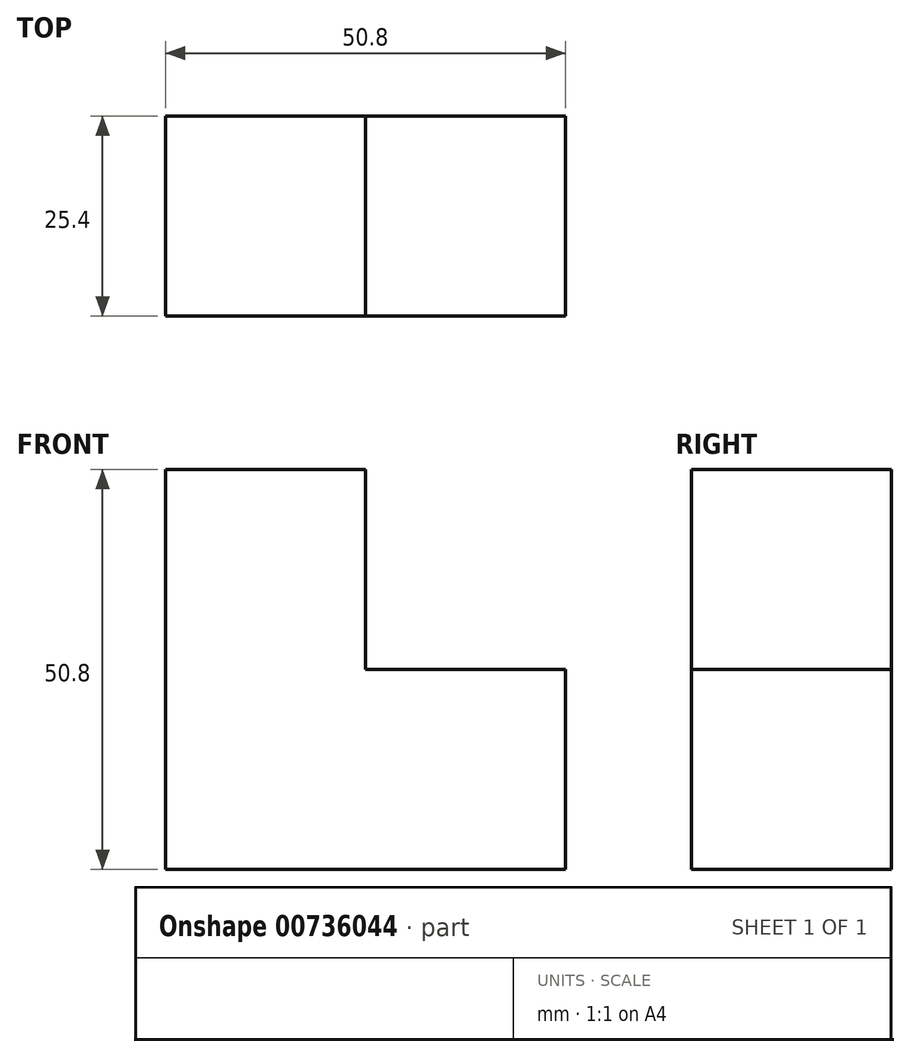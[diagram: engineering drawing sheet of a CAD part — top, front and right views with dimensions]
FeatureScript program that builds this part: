
annotation { "Feature Type Name" : "Feature", "Feature Type Description" : "" }
export const myFeature = defineFeature(function(context is Context, id is Id, definition is map)
    precondition{}
    {
        {
            var Q0;
            Q0=qCreatedBy(makeId("Front.planeOp"),FACE);
            var sketch = newSketch(context, id + "F0", { "sketchPlane" : qUnion([Q0])});
            skLineSegment(sketch, "E0", {"start": v(-41.15, 50.8) * mm, "end": v(-41.15, 0) * mm});
            skLineSegment(sketch, "E1", {"start": v(-41.15, 0) * mm, "end": v(9.65, 0) * mm});
            skLineSegment(sketch, "E2", {"start": v(-41.15, 50.8) * mm, "end": v(-15.75, 50.8) * mm});
            skLineSegment(sketch, "E3", {"start": v(-15.75, 50.8) * mm, "end": v(-15.75, 25.4) * mm});
            skLineSegment(sketch, "E4", {"start": v(-15.75, 25.4) * mm, "end": v(9.65, 25.4) * mm});
            skLineSegment(sketch, "E5", {"start": v(9.65, 25.4) * mm, "end": v(9.65, 0) * mm});
            skSolve(sketch);
        }
        {
            var Q0;
            Q0=qSketchRegion(id+"F0",true);
            extrude(context, id + "F1", {"entities" : qUnion([Q0]), "depth" : 25.4 * mm, "offsetDistance" : 25.4 * mm});
        }
    });
